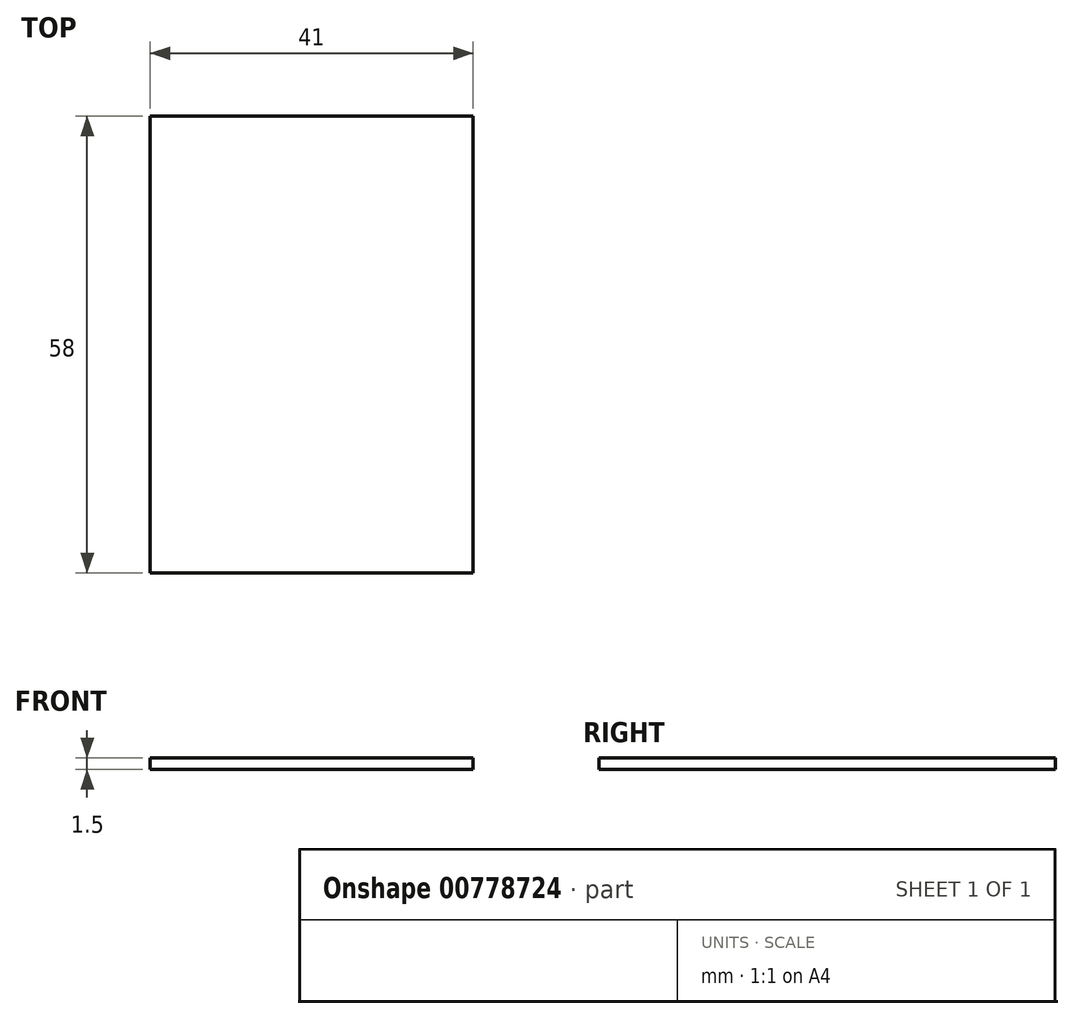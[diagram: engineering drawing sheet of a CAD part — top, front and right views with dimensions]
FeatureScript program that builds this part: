
annotation { "Feature Type Name" : "Feature", "Feature Type Description" : "" }
export const myFeature = defineFeature(function(context is Context, id is Id, definition is map)
    precondition{}
    {
        {
            var Q0;
            Q0=qCreatedBy(makeId("Top.planeOp"),FACE);
            var sketch = newSketch(context, id + "F0", { "sketchPlane" : qUnion([Q0])});
            skLineSegment(sketch, "E0.bottom", {"start": v(20.5, -29) * mm, "end": v(-20.5, -29) * mm});
            skLineSegment(sketch, "E0.top", {"start": v(20.5, 29) * mm, "end": v(-20.5, 29) * mm});
            skLineSegment(sketch, "E0.left", {"start": v(20.5, -29) * mm, "end": v(20.5, 29) * mm});
            skLineSegment(sketch, "E0.right", {"start": v(-20.5, -29) * mm, "end": v(-20.5, 29) * mm});
            skPoint(sketch, "E0.middle", {"position": v(0, 0) * mm});
            skSolve(sketch);
        }
        {
            var Q0;
            Q0=makeQuery(id+"F0.imprint","IMPRINT",FACE,{"disambiguationData":[TD([[makeQuery(id+"F0.imprint","IMPRINT",EDGE,{"derivedFrom":sQuery(id+"F0.wireOp",EDGE,"E0.bottom")}),-1.0]])]});
            extrude(context, id + "F1", {"entities" : qUnion([Q0]), "depth" : 1.5 * mm, "offsetDistance" : 25 * mm});
        }
    });
